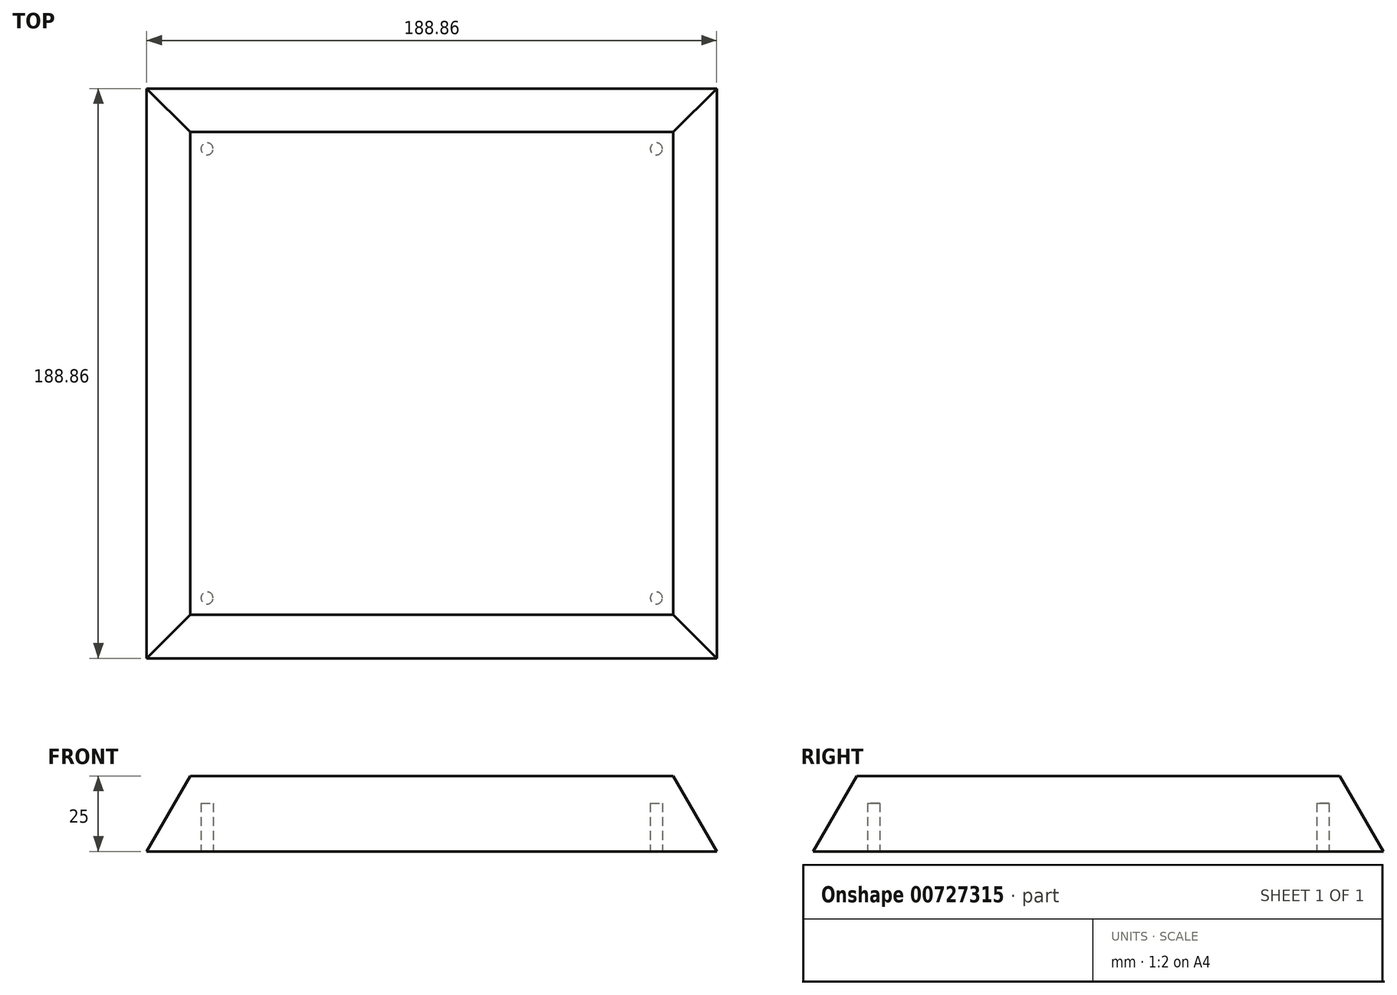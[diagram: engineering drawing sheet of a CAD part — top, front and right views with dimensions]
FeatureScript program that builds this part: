
annotation { "Feature Type Name" : "Feature", "Feature Type Description" : "" }
export const myFeature = defineFeature(function(context is Context, id is Id, definition is map)
    precondition{}
    {
        {
            var Q0;
            Q0=qCreatedBy(makeId("Top.planeOp"),FACE);
            var sketch = newSketch(context, id + "F0", { "sketchPlane" : qUnion([Q0])});
            skLineSegment(sketch, "E0.bottom", {"start": v(-80, 80) * mm, "end": v(80, 80) * mm});
            skLineSegment(sketch, "E0.top", {"start": v(-80, -80) * mm, "end": v(80, -80) * mm});
            skLineSegment(sketch, "E0.left", {"start": v(-80, 80) * mm, "end": v(-80, -80) * mm});
            skLineSegment(sketch, "E0.right", {"start": v(80, 80) * mm, "end": v(80, -80) * mm});
            skPoint(sketch, "E0.middle", {"position": v(0, 0) * mm});
            skSolve(sketch);
        }
        {
            var Q0;
            Q0=makeQuery(id+"F0.imprint","IMPRINT",FACE,{"disambiguationData":[TD([[makeQuery(id+"F0.imprint","IMPRINT",EDGE,{"derivedFrom":sQuery(id+"F0.wireOp",EDGE,"E0.bottom")}),-1.0]])]});
            extrude(context, id + "F1", {"entities" : qUnion([Q0]), "oppositeDirection" : true, "depth" : 25 * mm, "hasDraft" : true, "draftAngle" : 30 * degree});
        }
        {
            var Q0;
            Q0=makeQuery(id+"F1.opExtrude","CAP_FACE",FACE,{"disambiguationData":[OSD([sQuery(id+"F0.wireOp",EDGE,"E0.bottom"),sQuery(id+"F0.wireOp",EDGE,"E0.top"),sQuery(id+"F0.wireOp",EDGE,"E0.left"),sQuery(id+"F0.wireOp",EDGE,"E0.right")])],"isStart":false});
            var sketch = newSketch(context, id + "F2", { "sketchPlane" : qUnion([Q0])});
            skCircle(sketch, "E1", {"center": v(-74.43, -74.43) * mm, "radius": 2 * mm});
            skCircle(sketch, "E2", {"center": v(-74.43, 74.43) * mm, "radius": 2 * mm});
            skCircle(sketch, "E3", {"center": v(74.43, -74.43) * mm, "radius": 2 * mm});
            skCircle(sketch, "E4", {"center": v(74.43, 74.43) * mm, "radius": 2 * mm});
            skSolve(sketch);
        }
        {
            var Q0;
            Q0=makeQuery(id+"F2.imprint","IMPRINT",FACE,{"disambiguationData":[TD([[makeQuery(id+"F2.imprint","IMPRINT",EDGE,{"derivedFrom":sQuery(id+"F2.wireOp",EDGE,"E1")}),1.0]])]});
            var Q1;
            Q1=makeQuery(id+"F2.imprint","IMPRINT",FACE,{"disambiguationData":[TD([[makeQuery(id+"F2.imprint","IMPRINT",EDGE,{"derivedFrom":sQuery(id+"F2.wireOp",EDGE,"E2")}),1.0]])]});
            var Q2;
            Q2=makeQuery(id+"F2.imprint","IMPRINT",FACE,{"disambiguationData":[TD([[makeQuery(id+"F2.imprint","IMPRINT",EDGE,{"derivedFrom":sQuery(id+"F2.wireOp",EDGE,"E4")}),1.0]])]});
            var Q3;
            Q3=makeQuery(id+"F2.imprint","IMPRINT",FACE,{"disambiguationData":[TD([[makeQuery(id+"F2.imprint","IMPRINT",EDGE,{"derivedFrom":sQuery(id+"F2.wireOp",EDGE,"E3")}),1.0]])]});
            extrude(context, id + "F3", {"entities" : qUnion([Q0, Q1, Q2, Q3]), "operationType" : NewBodyOperationType.REMOVE, "oppositeDirection" : true, "depth" : 16 * mm});
        }
    });
